# Revit family: SKSMUKabelrinne SKS-Magic® 60 ungelocht FS_FT_A2_610_615_620_630_640_650_660
name_source: partatom
category: Generic Models
revit_build: Autodesk Revit 2017 (Build: 20190508_0315(x64)
units: mm (PartAtom-declared; Revit-internal decimal feet)

## family parameters
Always vertical = Yes
Can host rebar = No
Cut with Voids When Loaded = No
Part Type = Normal
Room Calculation Point = No
Round Connector Dimension = Use Diameter
Shared = No
Work Plane-Based = No

## types (20) — shared parameters
Cut's number = 2
Length = 3050 mm  [stored 10.0066 ft]
Length 1 = 3000 mm  [stored 9.84252 ft]
Length 2 = 50 mm  [stored 0.164042 ft]
Manufacturer = OBO BETTERMANN
URL = http://www.obo-bettermann.com
Width 2 = 7 mm  [stored 0.0229659 ft]

## per-type parameters (varying)
| type | GTIN | Manufacturer Art.No. | Material | Width | Width 1 |
| SKSMU 610 FS | 4012195829843 | 6059688 | Strip-galvanised | 100 mm  [stored 0.328084 ft] | 50 mm  [stored 0.164042 ft] |
| SKSMU 615 FS | 4012195829850 | 6059690 | Strip-galvanised | 150 mm | 75 mm |
| SKSMU 620 FS | 4012195829867 | 6059692 | Strip-galvanised | 200 mm  [stored 0.656168 ft] | 100 mm  [stored 0.328084 ft] |
| SKSMU 630 FS | 4012195829874 | 6059694 | Hot-dip galvanised | 300 mm | 150 mm |
| SKSMU 640 FS | 4012195829881 | 6059696 | Hot-dip galvanised | 400 mm  [stored 1.31234 ft] | 200 mm  [stored 0.656168 ft] |
| SKSMU 650 FS | 4012195829898 | 6059698 | Strip-galvanised | 500 mm  [stored 1.64042 ft] | 250 mm  [stored 0.82021 ft] |
| SKSMU 660 FS | 4012195829904 | 6059700 | Strip-galvanised | 600 mm | 300 mm |
| SKSMU 610 A2 | 4012195830689 | 6059722 | Edelstahl, rostfrei 1.4301 | 100 mm  [stored 0.328084 ft] | 50 mm  [stored 0.164042 ft] |
| SKSMU 620 A2 | 4012195830702 | 6059726 | Edelstahl, rostfrei 1.4301 | 200 mm  [stored 0.656168 ft] | 100 mm  [stored 0.328084 ft] |
| SKSMU 630 A2 | 4012195830740 | 6059728 | Edelstahl, rostfrei 1.4301 | 300 mm | 150 mm |
| SKSMU 640 A2 | 4012195830757 | 6059730 | Edelstahl, rostfrei 1.4301 | 400 mm  [stored 1.31234 ft] | 200 mm  [stored 0.656168 ft] |
| SKSMU 650 A2 | 4012195830764 | 6059732 | Edelstahl, rostfrei 1.4301 | 500 mm  [stored 1.64042 ft] | 250 mm  [stored 0.82021 ft] |
| SKSMU 660 A2 | 4012195830795 | 6059734 | Edelstahl, rostfrei 1.4301 | 600 mm | 300 mm |
| SKSMU 610 FT | 4012195829911 | 6059705 | Hot-dip galvanised | 100 mm  [stored 0.328084 ft] | 50 mm  [stored 0.164042 ft] |
| SKSMU 615 FT | 4012195829928 | 6059707 | Hot-dip galvanised | 150 mm | 75 mm |
| SKSMU 620 FT | 4012195830634 | 6059709 | Hot-dip galvanised | 200 mm  [stored 0.656168 ft] | 100 mm  [stored 0.328084 ft] |
| SKSMU 650 FT | 4012195830665 | 6059715 | Hot-dip galvanised | 500 mm  [stored 1.64042 ft] | 250 mm  [stored 0.82021 ft] |
| SKSMU 660 FT | 4012195830672 | 6059717 | Hot-dip galvanised | 600 mm | 300 mm |
| SKSMU 630 FT | 4012195830641 | 6059711 | Hot-dip galvanised | 300 mm | 150 mm |
| SKSMU 640 FT | 4012195830658 | 6059713 | Hot-dip galvanised | 400 mm  [stored 1.31234 ft] | 200 mm  [stored 0.656168 ft] |

note: column(s) folded — value = type name in every type: Article Type

note: [stored X ft] marks values corroborated as IEEE doubles in the binary element streams (Revit-internal decimal feet)

## geometry (parser evidence)
native form markers: Sweep x1
no freeform markers — native parametric forms only
